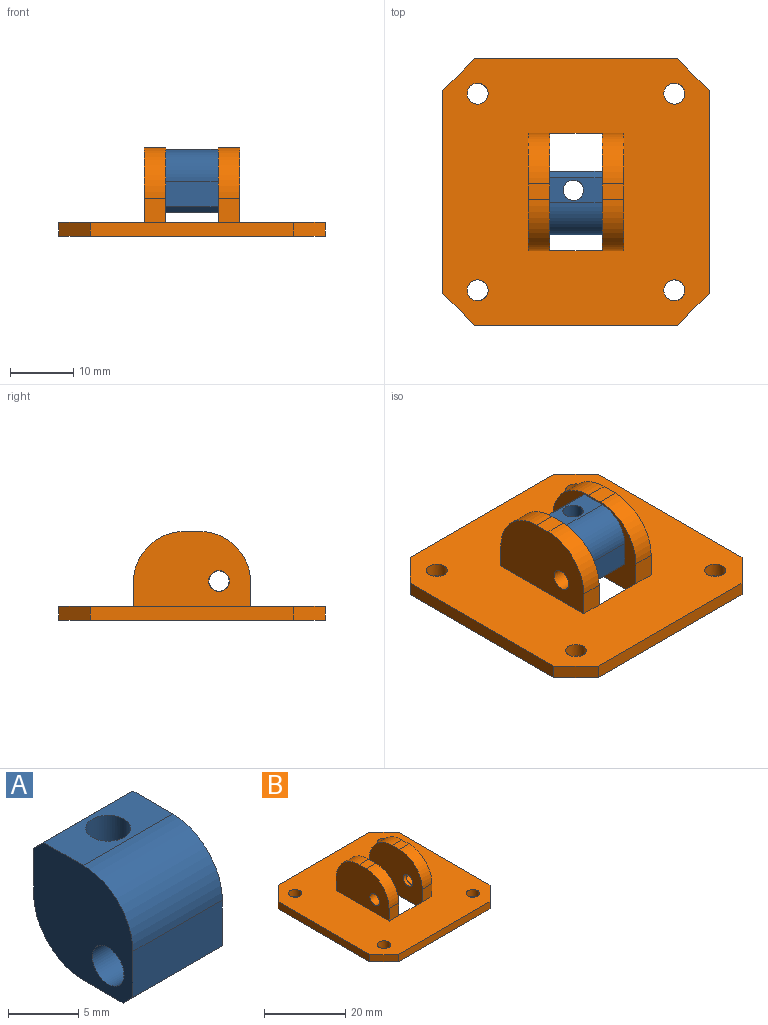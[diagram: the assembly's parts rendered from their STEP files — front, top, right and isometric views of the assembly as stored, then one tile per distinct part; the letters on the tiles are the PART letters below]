
ASSEMBLY  parts=2 mates=1
PART A: 14 faces, bbox 9x10x10 mm
  f0: cylinder r=1.6mm len=7mm, axis (0,0,-1), area 70.4mm2, adj f6,f11
  f1: plane 9x4mm, normal (0,0,-1), area 32.9mm2, adj f2,f4,f9,f10,f12
  f2: plane 10x10mm, normal (-1,0,0), area 80.2mm2, adj f1,f3,f5,f6,f7,f8,f9,f12
  f3: plane 9x4mm, normal (0,-1,0), area 36mm2, adj f2,f4,f8,f12
  f4: plane 10x10mm, normal (1,0,0), area 80.2mm2, adj f1,f3,f5,f6,f7,f8,f9,f12
  f5: plane 9x4mm, normal (0,1,0), area 36mm2, adj f2,f4,f9,f13
  f6: plane 9x4mm, normal (0,0,1), area 28mm2, adj f0,f2,f4,f8,f13
  f7: cylinder r=1.6mm len=9mm, axis (1,0,0), area 89.1mm2, adj f2,f4,f10,f11
  f8: cylinder r=5mm len=9mm, axis (-1,0,0), area 70.7mm2, adj f2,f3,f4,f6
  f9: cylinder r=5mm len=9mm, axis (-1,0,0), area 40.8mm2, adj f1,f2,f4,f5,f10,f11
  f10: cylinder r=3mm len=6mm, axis (0,0,-1), area 35.6mm2, adj f1,f7,f9,f11
  f11: plane 6x5.56mm, normal (0,0,-1), area 19.4mm2, adj f0,f7,f9,f10
  f12: plane 9x1mm, normal (0,-0.71,-0.71), area 12.7mm2, adj f1,f2,f3,f4
  f13: plane 9x1mm, normal (0,0.71,0.71), area 12.7mm2, adj f2,f4,f5,f6
PART B: 39 faces, bbox 42x42x14 mm
  f0: cylinder r=1.65mm len=3.3mm, axis (1,0,0), area 10.4mm2, adj f2,f38
  f1: plane 8.2x2.2mm, normal (0,-1,0), area 18mm2, adj f2,f8,f9,f10
  f2: plane 18.5x14mm, normal (-1,0,0), area 223mm2, adj f0,f1,f3,f10,f15,f17,f18,f19
  f3: plane 8.2x2.2mm, normal (0,1,0), area 18mm2, adj f2,f8,f9,f10
  f4: plane 32x2.2mm, normal (0,-1,0), area 70.4mm2, adj f9,f10,f29,f30
  f5: plane 32x2.2mm, normal (1,0,0), area 70.4mm2, adj f9,f10,f30,f31
  f6: plane 32x2.2mm, normal (0,1,0), area 70.4mm2, adj f9,f10,f28,f31
  f7: plane 32x2.2mm, normal (-1,0,0), area 70.4mm2, adj f9,f10,f28,f29
  f8: plane 18.5x14mm, normal (1,0,0), area 223mm2, adj f1,f3,f10,f11,f12,f14,f21,f22
  f9: plane 42x42mm, normal (0,0,1), area 1402.3mm2, adj f1,f3,f4,f5,f6,f7,f11,f12
  f10: plane 42x42mm, normal (0,0,-1), area 1528.1mm2, adj f1,f2,f3,f4,f5,f6,f7,f8
  f11: plane 3.8x3.4mm, normal (0,-1,0), area 12.9mm2, adj f8,f9,f13,f22
  f12: plane 3.8x3.4mm, normal (0,1,0), area 12.9mm2, adj f8,f9,f13,f21
  f13: plane 18.5x11.8mm, normal (-1,0,0), area 182.3mm2, adj f9,f11,f12,f14,f21,f22,f23
  f14: plane 3.4x2.5mm, normal (0,0,1), area 8.5mm2, adj f8,f13,f21,f22
  f15: plane 3.8x3.4mm, normal (0,-1,0), area 12.9mm2, adj f2,f9,f16,f20
  f16: plane 18.5x11.8mm, normal (1,0,0), area 159.7mm2, adj f9,f15,f17,f18,f19,f20,f32,f33
  f17: plane 3.8x3.4mm, normal (0,1,0), area 12.9mm2, adj f2,f9,f16,f19
  f18: plane 3.4x2.5mm, normal (0,0,1), area 8.5mm2, adj f2,f16,f19,f20
  f19: cylinder r=8mm len=8mm, axis (1,0,0), area 42.7mm2, adj f2,f16,f17,f18
  f20: cylinder r=8mm len=8mm, axis (-1,0,0), area 42.7mm2, adj f2,f15,f16,f18
  f21: cylinder r=8mm len=8mm, axis (1,0,0), area 42.7mm2, adj f8,f12,f13,f14
  f22: cylinder r=8mm len=8mm, axis (-1,0,0), area 42.7mm2, adj f8,f11,f13,f14
  f23: cylinder r=1.65mm len=3.4mm, axis (1,0,0), area 35.2mm2, adj f8,f13
  f24: cylinder r=1.65mm len=3.3mm, axis (0,0,-1), area 22.8mm2, adj f9,f10
  f25: cylinder r=1.65mm len=3.3mm, axis (0,0,-1), area 22.8mm2, adj f9,f10
  f26: cylinder r=1.65mm len=3.3mm, axis (0,0,-1), area 22.8mm2, adj f9,f10
  f27: cylinder r=1.65mm len=3.3mm, axis (0,0,-1), area 22.8mm2, adj f9,f10
  f28: plane 5x5mm, normal (-0.71,0.71,0), area 15.6mm2, adj f6,f7,f9,f10
  f29: plane 5x5mm, normal (-0.71,-0.71,0), area 15.6mm2, adj f4,f7,f9,f10
  f30: plane 5x5mm, normal (0.71,-0.71,0), area 15.6mm2, adj f4,f5,f9,f10
  f31: plane 5x5mm, normal (0.71,0.71,0), area 15.6mm2, adj f5,f6,f9,f10
  f32: plane 3x2.4mm, normal (0,0.5,-0.87), area 8.3mm2, adj f16,f33,f37,f38
  f33: plane 3.46x2.4mm, normal (0,1,0), area 8.3mm2, adj f16,f32,f34,f38
  f34: plane 3x2.4mm, normal (0,0.5,0.87), area 8.3mm2, adj f16,f33,f35,f38
  f35: plane 3x2.4mm, normal (0,-0.5,0.87), area 8.3mm2, adj f16,f34,f36,f38
  f36: plane 3.46x2.4mm, normal (0,-1,0), area 8.3mm2, adj f16,f35,f37,f38
  f37: plane 3x2.4mm, normal (0,-0.5,-0.87), area 8.3mm2, adj f16,f32,f36,f38
  f38: plane 6.93x6mm, normal (1,0,0), area 22.6mm2, adj f0,f32,f33,f34,f35,f36,f37
PLACE A t=(-0.91,-2.07,0.26)mm
PLACE B t=(3.99,4.68,-3.44)mm
MATE fastened A.f7 <-> B.f0  axis (1,0,0) through (8.09,0.43,2.76)mm
